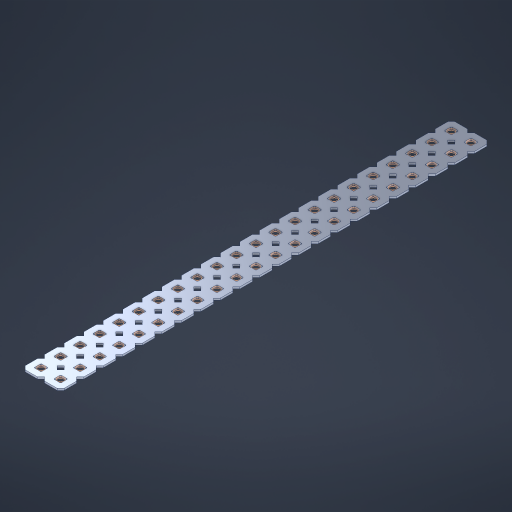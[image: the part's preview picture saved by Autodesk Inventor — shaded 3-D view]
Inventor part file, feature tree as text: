
AUTODESK INVENTOR PART (.ipt)
format: ipt  version: 2023 (Build 270158000, 158)  size: 768,000 bytes
history: native  units: in
note: dims shown in document units (in); Inventor stores cm internally (conversion verified against a paired STEP export)
features: other x45, extrude x43, sketch x2, pattern_linear x1
ambient origin geometry x8: Origin, YZ Plane, XZ Plane, XY Plane, X Axis, Y Axis, Z Axis, Center Point
bodies: Solid1 (feature_tree), Body (feature_tree)
feature tree (91):
  pattern_linear  "Rectangular Pattern1"  Spacing1=0.09in  [1 undecoded]
  sketch  "Sketch1"  dims[d1=0.5in]
  sketch  "Sketch2"  dims[d2=0.182in d3=0.09in d4=0.09in d5=0.09in d6=0.09in d7=0.09in d8=0.09in d9=0.09in d10=0.09in d11=0.02in d13=0.0in d14=0.172in d15=0.0625in d16=0.0in d19=0.5in d22=0.5in]
  other  "Srf1"
  other  "Srf126"
  other  "Srf127"
  other  "Srf128"
  other  "Srf129"
  other  "Srf130"
  other  "Srf131"
  other  "Srf250"
  other  "Srf251"
  other  "Srf252"
  other  "Srf253"
  other  "Srf254"
  other  "Srf255"
  other  "Srf256"
  other  "Srf257"
  other  "Srf258"
  other  "Srf259"
  other  "Srf260"
  other  "Srf261"
  other  "Srf262"
  other  "Srf263"
  other  "Srf264"
  other  "Srf268"
  other  "Srf269"
  other  "Srf270"
  other  "Srf271"
  other  "Srf272"
  other  "Srf273"
  other  "Srf274"
  other  "Srf275"
  other  "Srf276"
  other  "Srf277"
  other  "Srf278"
  other  "Srf279"
  other  "Srf280"
  other  "Srf281"
  other  "Srf282"
  other  "Srf283"
  other  "Srf284"
  other  "Srf285"
  other  "Srf286"
  other  "Srf287"
  other  "Srf288"
  other  "Srf289"
  other  "Circle"
  extrude  "ExtrusionSrf126"  Depth=0.09in
  extrude  "ExtrusionSrf127"  Depth=0.09in
  extrude  "ExtrusionSrf128"  Depth=0.09in
  extrude  "ExtrusionSrf129"  Depth=0.09in
  extrude  "ExtrusionSrf130"  Depth=0.09in
  extrude  "ExtrusionSrf131"  Depth=0.09in
  extrude  "ExtrusionSrf250"  Depth=0.09in
  extrude  "ExtrusionSrf251"  Depth=0.02in
  extrude  "ExtrusionSrf252"  TaperAngle=0.0deg  [1 undecoded]
  extrude  "ExtrusionSrf253"  Depth=0.5in
  extrude  "ExtrusionSrf254"  Depth=0.5in TaperAngle=0.0deg
  extrude  "ExtrusionSrf255"  Depth=0.5in
  extrude  "ExtrusionSrf256"  Depth=0.5in
  extrude  "ExtrusionSrf257"  [1 undecoded]
  extrude  "ExtrusionSrf258"  [1 undecoded]
  extrude  "ExtrusionSrf259"  [1 undecoded]
  extrude  "ExtrusionSrf260"  [1 undecoded]
  extrude  "ExtrusionSrf261"  [1 undecoded]
  extrude  "ExtrusionSrf262"  [1 undecoded]
  extrude  "ExtrusionSrf263"  [1 undecoded]
  extrude  "ExtrusionSrf264"  [1 undecoded]
  extrude  "ExtrusionSrf268"  [1 undecoded]
  extrude  "ExtrusionSrf269"  [1 undecoded]
  extrude  "ExtrusionSrf270"  [1 undecoded]
  extrude  "ExtrusionSrf271"  [1 undecoded]
  extrude  "ExtrusionSrf272"  [1 undecoded]
  extrude  "ExtrusionSrf273"  [1 undecoded]
  extrude  "ExtrusionSrf274"  [1 undecoded]
  extrude  "ExtrusionSrf275"  [1 undecoded]
  extrude  "ExtrusionSrf276"  [1 undecoded]
  extrude  "ExtrusionSrf277"  [1 undecoded]
  extrude  "ExtrusionSrf278"  [1 undecoded]
  extrude  "ExtrusionSrf279"  [1 undecoded]
  extrude  "ExtrusionSrf280"  [1 undecoded]
  extrude  "ExtrusionSrf281"  [1 undecoded]
  extrude  "ExtrusionSrf282"  [1 undecoded]
  extrude  "ExtrusionSrf283"  [1 undecoded]
  extrude  "ExtrusionSrf284"  [1 undecoded]
  extrude  "ExtrusionSrf285"  [1 undecoded]
  extrude  "ExtrusionSrf286"  [1 undecoded]
  extrude  "ExtrusionSrf287"  [1 undecoded]
  extrude  "ExtrusionSrf288"  [1 undecoded]
  extrude  "ExtrusionSrf289"  [1 undecoded]
note: 32 required parameter values undecoded (feature->parameter linkage not recoverable at this tier; creation-order binding heuristic only, values carry confidence <= 0.55)
